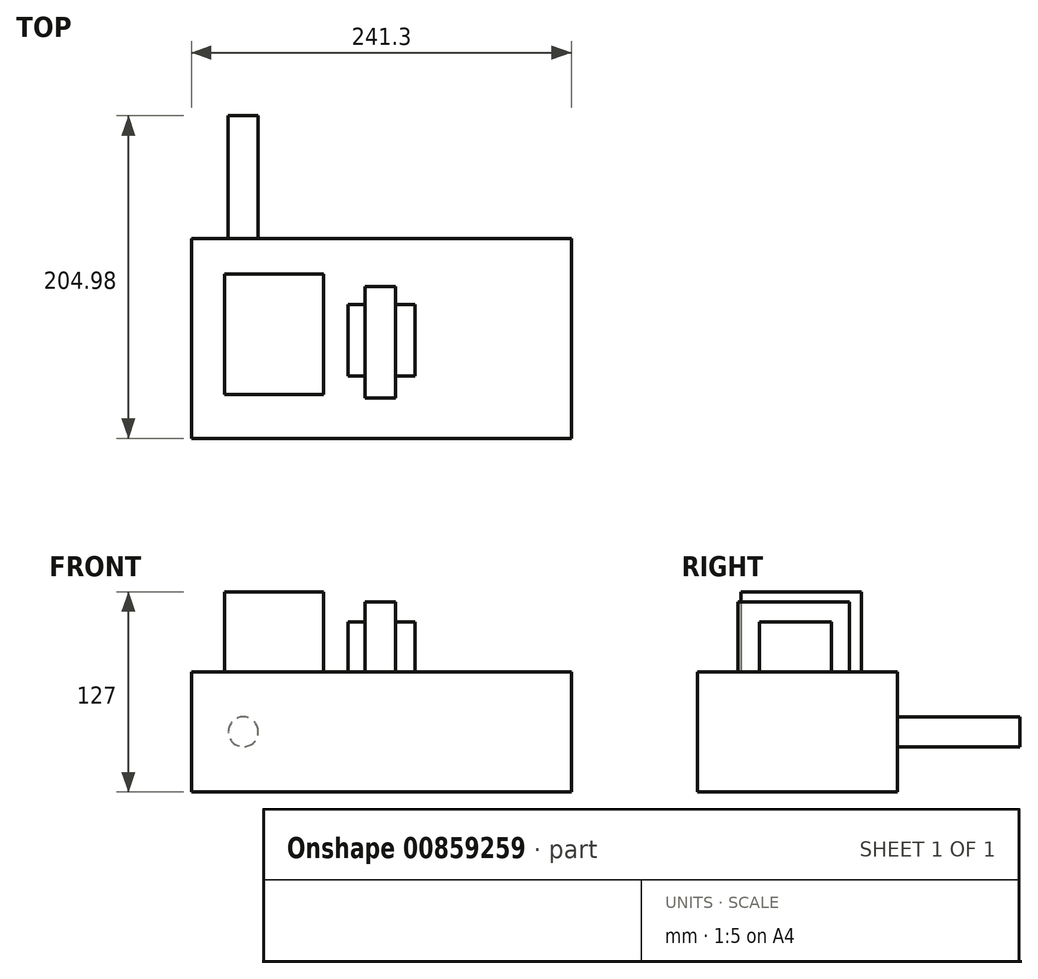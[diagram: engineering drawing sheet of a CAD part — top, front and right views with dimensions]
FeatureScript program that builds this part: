
annotation { "Feature Type Name" : "Feature", "Feature Type Description" : "" }
export const myFeature = defineFeature(function(context is Context, id is Id, definition is map)
    precondition{}
    {
        {
            var Q0;
            Q0=qCreatedBy(makeId("Front.planeOp"),FACE);
            var sketch = newSketch(context, id + "F0", { "sketchPlane" : qUnion([Q0])});
            skLineSegment(sketch, "E0.bottom", {"start": v(-120.65, 38.1) * mm, "end": v(120.65, 38.1) * mm});
            skLineSegment(sketch, "E0.top", {"start": v(-120.65, -38.1) * mm, "end": v(120.65, -38.1) * mm});
            skLineSegment(sketch, "E0.left", {"start": v(-120.65, 38.1) * mm, "end": v(-120.65, -38.1) * mm});
            skLineSegment(sketch, "E0.right", {"start": v(120.65, 38.1) * mm, "end": v(120.65, -38.1) * mm});
            skPoint(sketch, "E0.middle", {"position": v(0, 0) * mm});
            skSolve(sketch);
        }
        {
            var Q0;
            Q0 = qSketchRegion(id + "F0", true);
            extrude(context, id + "F1", {"entities" : qUnion([Q0]), "oppositeDirection" : true, "depth" : 127 * mm, "offsetDistance" : 25.4 * mm});
        }
        {
            var Q0;
            Q0=makeQuery(id+"F1.opExtrude","SWEPT_FACE",FACE,{"disambiguationData":[OSD([sQuery(id+"F0.wireOp",EDGE,"E0.bottom")])]});
            var sketch = newSketch(context, id + "F2", { "sketchPlane" : qUnion([Q0])});
            skLineSegment(sketch, "E1.bottom", {"start": v(-99.63, 27.8) * mm, "end": v(-36.8, 27.8) * mm});
            skLineSegment(sketch, "E1.top", {"start": v(-99.63, 104.25) * mm, "end": v(-36.8, 104.25) * mm});
            skLineSegment(sketch, "E1.left", {"start": v(-99.63, 27.8) * mm, "end": v(-99.63, 104.25) * mm});
            skLineSegment(sketch, "E1.right", {"start": v(-36.8, 27.8) * mm, "end": v(-36.8, 104.25) * mm});
            skSolve(sketch);
        }
        {
            var Q0;
            Q0 = qSketchRegion(id + "F2", true);
            extrude(context, id + "F3", {"entities" : qUnion([Q0]), "operationType" : NewBodyOperationType.ADD, "depth" : 50.8 * mm, "offsetDistance" : 25.4 * mm});
        }
        {
            var Q0;
            Q0=makeQuery(id+"F1.opExtrude","SWEPT_FACE",FACE,{"disambiguationData":[OSD([sQuery(id+"F0.wireOp",EDGE,"E0.bottom")])]});
            var sketch = newSketch(context, id + "F4", { "sketchPlane" : qUnion([Q0])});
            skLineSegment(sketch, "E2.bottom", {"start": v(-10.37, 25.72) * mm, "end": v(8.95, 25.72) * mm});
            skLineSegment(sketch, "E2.top", {"start": v(-10.37, 96.59) * mm, "end": v(8.95, 96.59) * mm});
            skLineSegment(sketch, "E2.left", {"start": v(-10.37, 25.72) * mm, "end": v(-10.37, 96.59) * mm});
            skLineSegment(sketch, "E2.right", {"start": v(8.95, 25.72) * mm, "end": v(8.95, 96.59) * mm});
            skSolve(sketch);
        }
        {
            var Q0;
            Q0 = qSketchRegion(id + "F4", true);
            extrude(context, id + "F5", {"entities" : qUnion([Q0]), "operationType" : NewBodyOperationType.ADD, "depth" : 44.45 * mm, "offsetDistance" : 25.4 * mm});
        }
        {
            var Q0;
            Q0=makeQuery(id+"F1.opExtrude","SWEPT_FACE",FACE,{"disambiguationData":[OSD([sQuery(id+"F0.wireOp",EDGE,"E0.bottom")])]});
            var sketch = newSketch(context, id + "F6", { "sketchPlane" : qUnion([Q0])});
            skLineSegment(sketch, "E3.bottom", {"start": v(-10.37, 39.5) * mm, "end": v(-21.16, 39.5) * mm});
            skLineSegment(sketch, "E3.top", {"start": v(-10.37, 85.07) * mm, "end": v(-21.16, 85.07) * mm});
            skLineSegment(sketch, "E3.left", {"start": v(-10.37, 39.5) * mm, "end": v(-10.37, 85.07) * mm});
            skLineSegment(sketch, "E3.right", {"start": v(-21.16, 39.5) * mm, "end": v(-21.16, 85.07) * mm});
            skLineSegment(sketch, "E4.bottom", {"start": v(8.95, 39.56) * mm, "end": v(21.28, 39.56) * mm});
            skLineSegment(sketch, "E4.top", {"start": v(8.95, 85.07) * mm, "end": v(21.28, 85.07) * mm});
            skLineSegment(sketch, "E4.left", {"start": v(8.95, 39.56) * mm, "end": v(8.95, 85.07) * mm});
            skLineSegment(sketch, "E4.right", {"start": v(21.28, 39.56) * mm, "end": v(21.28, 85.07) * mm});
            skSolve(sketch);
        }
        {
            var Q0;
            Q0 = qSketchRegion(id + "F6", true);
            extrude(context, id + "F7", {"entities" : qUnion([Q0]), "operationType" : NewBodyOperationType.ADD, "depth" : 31.75 * mm, "offsetDistance" : 25.4 * mm});
        }
        {
            var Q0;
            Q0=makeQuery(id+"F1.opExtrude","CAP_FACE",FACE,{"disambiguationData":[OSD([sQuery(id+"F0.wireOp",EDGE,"E0.bottom"),sQuery(id+"F0.wireOp",EDGE,"E0.top"),sQuery(id+"F0.wireOp",EDGE,"E0.left"),sQuery(id+"F0.wireOp",EDGE,"E0.right")])],"isStart":false});
            var sketch = newSketch(context, id + "F8", { "sketchPlane" : qUnion([Q0])});
            skCircle(sketch, "E5", {"center": v(87.7, 0) * mm, "radius": 9.53 * mm});
            skSolve(sketch);
        }
        {
            var Q0;
            Q0 = qSketchRegion(id + "F8", true);
            extrude(context, id + "F9", {"entities" : qUnion([Q0]), "operationType" : NewBodyOperationType.ADD, "depth" : 77.98 * mm, "offsetDistance" : 25.4 * mm});
        }
    });
